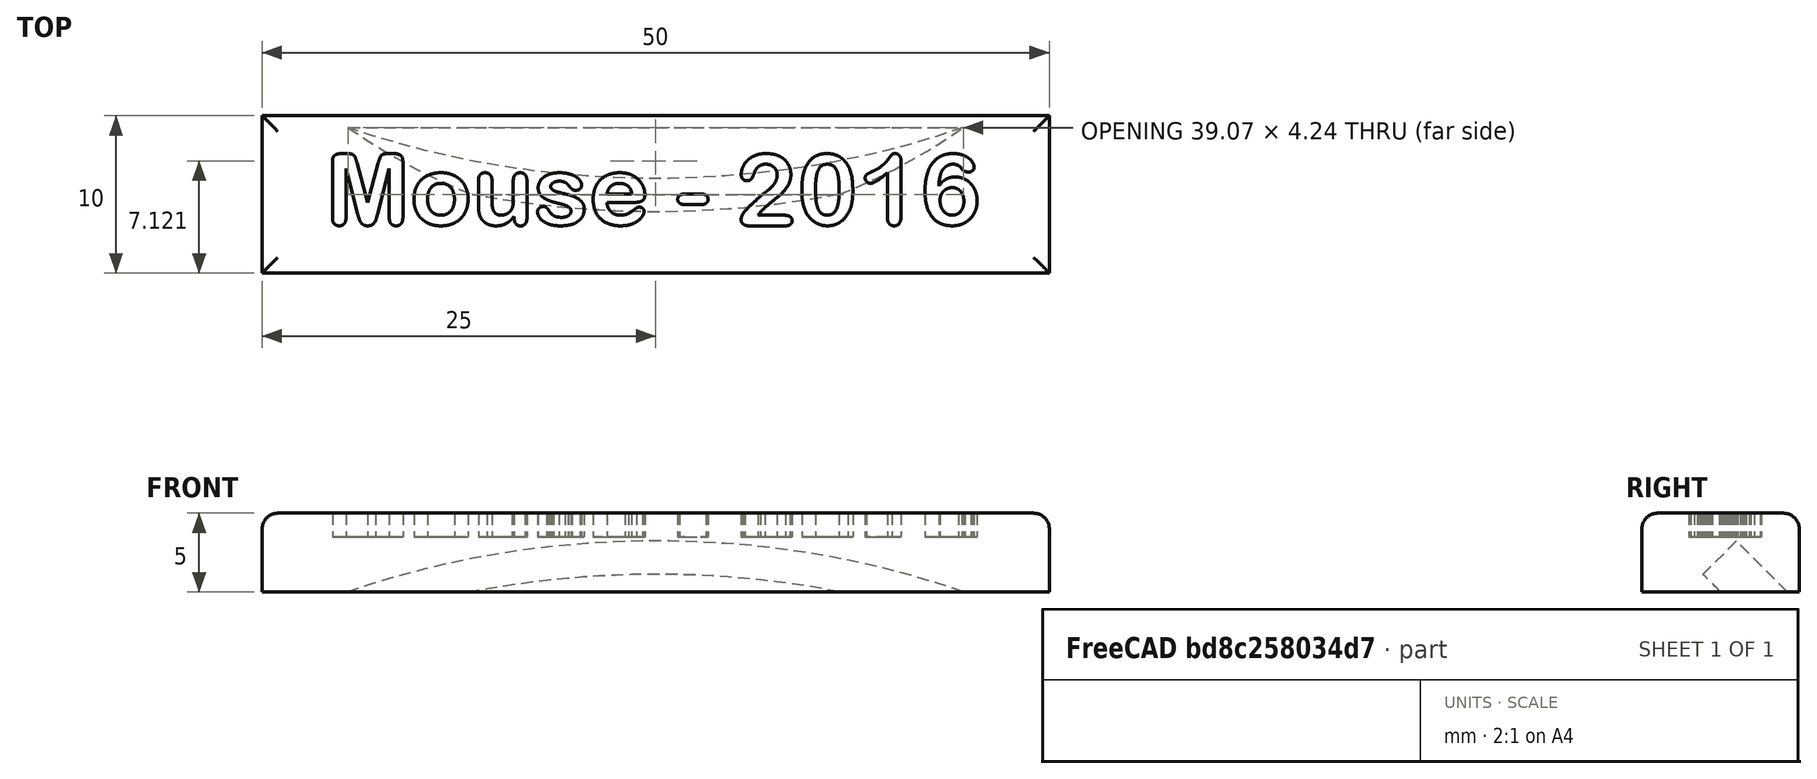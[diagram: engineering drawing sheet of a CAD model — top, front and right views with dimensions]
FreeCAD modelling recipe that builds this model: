
FCSTD DOCUMENT  (FreeCAD 0.19R24291 (Git))
Label: Name-Plate
License: All rights reserved
LicenseURL: http://en.wikipedia.org/wiki/All_rights_reserved
objects: Part::Part2DObjectPython×7, Sketcher::SketchObject×4, PartDesign::Pocket×3, PartDesign::Pad×2, PartDesign::Fillet×2, PartDesign::Body×2, Mesh::Feature×1, PartDesign::Plane×1
note: 28 computed .brp shape members not serialized (recipe doc carries the construction recipe); baked Part::Feature solids carry a one-line shape summary decoded from their .brp

FEATURE [Mesh::Feature] Ferret
  Placement = pos=(-125,-110,0) rot=(0,0,1;0rad)
FEATURE [Sketcher::SketchObject] Sketch
  FullyConstrained = true
  MapMode = 5
  Support = -> [XY_Plane]
  sketch-geometry (4):
    g0: LineSegment StartX=-25 StartY=0 StartZ=0 EndX=25 EndY=0 EndZ=0
    g1: LineSegment StartX=25 StartY=0 StartZ=0 EndX=25 EndY=-10 EndZ=0
    g2: LineSegment StartX=25 StartY=-10 StartZ=0 EndX=-25 EndY=-10 EndZ=0
    g3: LineSegment StartX=-25 StartY=-10 StartZ=0 EndX=-25 EndY=0 EndZ=0
  constraints (11):
    c: Coincident(g0,g1)
    c: Coincident(g1,g2)
    c: Coincident(g2,g3)
    c: Coincident(g3,g0)
    c: Horizontal(g0)
    c: Vertical(g1)
    c: Vertical(g3)
    c: PointOnObject(g0,g-1)
    c: Symmetric(g2,g1,g-2)
    c: DistanceY(g3,g3) = 10
    c: DistanceX(g2,g2) = 50
FEATURE [PartDesign::Pad] Pad
  Direction = (1,1,1)
  Length = 5
  Length2 = 100
  Profile = -> Sketch
  Type = 0
FEATURE [Part::Part2DObjectPython] ShapeString001  label="Trouble"  # Draft 2D object (typed FeaturePython)
  FontFile = /System/Library/Fonts/Supplemental/Arial Rounded Bold.ttf
  Size = 7
  String = Trouble - 2016
  Tracking = 0
FEATURE [Part::Part2DObjectPython] ShapeString002  label="Pretzel"  # Draft 2D object (typed FeaturePython)
  FontFile = /System/Library/Fonts/Supplemental/Arial Narrow Bold Italic.ttf
  Size = 7
  String = Pretzel - 2017
  Tracking = 0
FEATURE [Part::Part2DObjectPython] ShapeString003  label="Cajun"  # Draft 2D object (typed FeaturePython)
  FontFile = /System/Library/Fonts/Supplemental/Arial Narrow Bold Italic.ttf
  Size = 7
  String = Cajun - 2018
  Tracking = 0
FEATURE [Part::Part2DObjectPython] ShapeString004  label="Baguette"  # Draft 2D object (typed FeaturePython)
  FontFile = /System/Library/Fonts/Supplemental/Arial Narrow Bold Italic.ttf
  Size = 7
  String = Baguette - 2018
  Tracking = 0
FEATURE [Part::Part2DObjectPython] ShapeString005  label="Spice"  # Draft 2D object (typed FeaturePython)
  FontFile = /System/Library/Fonts/Supplemental/Arial Narrow Bold Italic.ttf
  Size = 7
  String = Spice - 2018
  Tracking = 0
FEATURE [Part::Part2DObjectPython] ShapeString006  label="Bunny"  # Draft 2D object (typed FeaturePython)
  FontFile = /System/Library/Fonts/Supplemental/Arial Narrow Bold Italic.ttf
  Size = 7
  String = Bunny - 2019
  Tracking = 0
FEATURE [Sketcher::SketchObject] Sketch001
  AttachmentOffset = pos=(0,-30,-25) rot=(1,0,0;0.785398rad)
  FullyConstrained = true
  MapMode = 5
  Placement = pos=(0,25,-30) rot=(1,0,0;2.35619rad)
  Support = -> [XZ_Plane]
  sketch-geometry (1):
    g0: Circle CenterX=0 CenterY=0 CenterZ=0 NormalX=0 NormalY=0 NormalZ=1 AngleXU=0 Radius=44
  constraints (2):
    c: Coincident(g0,g-1)
    c: Radius(g0) = 44
FEATURE [PartDesign::Pocket] Pocket
  BaseFeature = -> Pad
  Length = 3
  Length2 = 100
  Profile = -> Sketch001
  Type = 0
FEATURE [PartDesign::Fillet] Fillet
  Base = -> Pocket [Edge7,Edge16,Edge10,Edge4]
  BaseFeature = -> Pocket
  Radius = 1
  SupportTransform = false
FEATURE [PartDesign::Body] Body  label="Base Nameplace"
  Group = -> [Sketch,Pad,Sketch001,Pocket,Fillet]
  Origin = -> Origin
  Tip = -> Fillet
FEATURE [Sketcher::SketchObject] Sketch002
  AttachmentOffset = pos=(0,-30,-25) rot=(1,0,0;0.785398rad)
  FullyConstrained = true
  MapMode = 5
  Placement = pos=(0,25,-30) rot=(1,0,0;2.35619rad)
  Support = -> [XZ_Plane001]
  sketch-geometry (1):
    g0: Circle CenterX=0 CenterY=0 CenterZ=0 NormalX=0 NormalY=0 NormalZ=1 AngleXU=0 Radius=44
  constraints (2):
    c: Coincident(g0,g-1)
    c: Radius(g0) = 44
FEATURE [Sketcher::SketchObject] Sketch003
  FullyConstrained = true
  MapMode = 5
  Support = -> [XY_Plane001]
  sketch-geometry (4):
    g0: LineSegment StartX=-25 StartY=0 StartZ=0 EndX=25 EndY=0 EndZ=0
    g1: LineSegment StartX=25 StartY=0 StartZ=0 EndX=25 EndY=-10 EndZ=0
    g2: LineSegment StartX=25 StartY=-10 StartZ=0 EndX=-25 EndY=-10 EndZ=0
    g3: LineSegment StartX=-25 StartY=-10 StartZ=0 EndX=-25 EndY=0 EndZ=0
  constraints (11):
    c: Coincident(g0,g1)
    c: Coincident(g1,g2)
    c: Coincident(g2,g3)
    c: Coincident(g3,g0)
    c: Horizontal(g0)
    c: Vertical(g1)
    c: Vertical(g3)
    c: PointOnObject(g0,g-1)
    c: Symmetric(g2,g1,g-2)
    c: DistanceY(g3,g3) = 10
    c: DistanceX(g2,g2) = 50
FEATURE [PartDesign::Pad] Pad001
  Direction = (1,1,1)
  Length = 5
  Length2 = 100
  Profile = -> Sketch003
  Type = 0
FEATURE [PartDesign::Pocket] Pocket001
  BaseFeature = -> Pad001
  Length = 3
  Length2 = 100
  Profile = -> Sketch002
  Type = 0
FEATURE [PartDesign::Fillet] Fillet001
  Base = -> Pocket001 [Edge7,Edge16,Edge10,Edge4]
  BaseFeature = -> Pocket001
  Radius = 1
  SupportTransform = false
FEATURE [Part::Part2DObjectPython] ShapeString  label="Mouse"  # Draft 2D object (typed FeaturePython)
  AttachmentOffset = pos=(-21,-7,0) rot=(0,0,1;0rad)
  FontFile = /System/Library/Fonts/Supplemental/Arial Rounded Bold.ttf
  MapMode = 5
  Placement = pos=(-21,-7,5) rot=(0,0,1;0rad)
  Size = 5
  String = Mouse - 2016
  Support = -> [Fillet001]
  Tracking = 0
FEATURE [PartDesign::Pocket] Pocket002
  BaseFeature = -> Fillet001
  Length = 1.5
  Length2 = 100
  Profile = -> ShapeString
  Type = 0
FEATURE [PartDesign::Plane] DatumPlane
  Length = 60
  MapMode = 5
  Placement = pos=(0,0,5) rot=(0,0,1;0rad)
  ResizeMode = 0
  Support = -> [Fillet001]
  Width = 60
FEATURE [PartDesign::Body] Body001  label="Mouse Nameplate"
  Group = -> [Sketch003,Pad001,Sketch002,Pocket001,Fillet001,DatumPlane,ShapeString,Pocket002]
  Origin = -> Origin001
  Tip = -> Pocket002
